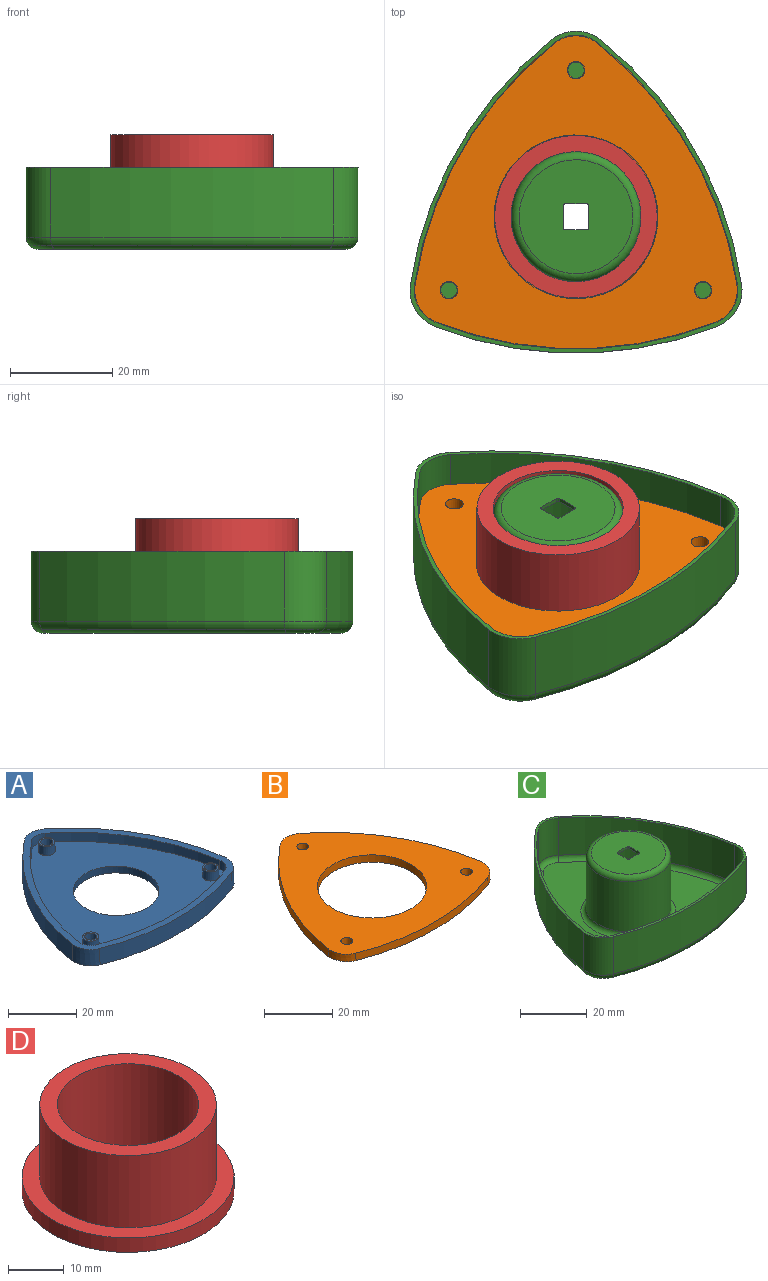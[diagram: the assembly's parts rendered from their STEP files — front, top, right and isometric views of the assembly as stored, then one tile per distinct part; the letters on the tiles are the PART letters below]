
ASSEMBLY  parts=4 mates=3
PART A: 25 faces, bbox 63.3x61.4x5.7 mm
  f0: plane 58.4x56.47mm, normal (0,0,1), area 1717.7mm2, adj f1,f8,f9,f10,f11,f12,f13,f17
  f1: cone r=12.66mm half-angle=3deg, axis (0,0,-1), area 201.3mm2, adj f0,f2
  f2: plane 63.31x61.38mm, normal (0,0,-1), area 2200.2mm2, adj f1,f3,f4,f5,f6,f7,f14,f16
  f3: cone r=6.83mm half-angle=2deg, axis (0,0,-1), area 51.7mm2, adj f2,f4,f14,f15
  f4: cone r=74.46mm half-angle=2deg, axis (0,0,-1), area 319.6mm2, adj f2,f3,f5,f15
  f5: cone r=6.83mm half-angle=2deg, axis (0,0,-1), area 51.7mm2, adj f2,f4,f6,f15
  f6: cone r=74.46mm half-angle=2deg, axis (0,0,-1), area 319.6mm2, adj f2,f5,f7,f15
  f7: cone r=6.83mm half-angle=2deg, axis (0,0,-1), area 51.7mm2, adj f2,f6,f14,f15
  f8: cone r=71.92mm half-angle=2deg, axis (0,0,1), area 172.1mm2, adj f0,f9,f13,f15
  f9: cone r=4.29mm half-angle=2deg, axis (0,0,1), area 18.9mm2, adj f0,f8,f10,f15
  f10: cone r=71.92mm half-angle=2deg, axis (0,0,1), area 172.1mm2, adj f0,f9,f11,f15
  f11: cone r=4.29mm half-angle=2deg, axis (0,0,1), area 18.9mm2, adj f0,f10,f12,f15
  f12: cone r=71.92mm half-angle=2deg, axis (0,0,1), area 172.1mm2, adj f0,f11,f13,f15
  f13: cone r=4.29mm half-angle=2deg, axis (0,0,1), area 18.9mm2, adj f0,f8,f12,f15
  f14: cone r=74.46mm half-angle=2deg, axis (0,0,-1), area 319.6mm2, adj f2,f3,f7,f15
  f15: plane 62.91x60.98mm, normal (0,0,1), area 401.3mm2, adj f3,f4,f5,f6,f7,f8,f9,f10
  f16: cone r=1.59mm half-angle=2deg, axis (0,0,1), area 60.6mm2, adj f2,f18
  f17: cone r=2.54mm half-angle=2deg, axis (0,0,-1), area 47.8mm2, adj f0,f18
  f18: plane 4.68x4.68mm, normal (0,0,1), area 7.2mm2, adj f16,f17
  f19: cone r=1.59mm half-angle=2deg, axis (0,0,1), area 60.6mm2, adj f2,f21
  f20: cone r=2.54mm half-angle=2deg, axis (0,0,-1), area 47.8mm2, adj f0,f21
  f21: plane 4.68x4.68mm, normal (0,0,1), area 7.2mm2, adj f19,f20
  f22: cone r=1.59mm half-angle=2deg, axis (0,0,1), area 60.6mm2, adj f2,f24
  f23: cone r=2.54mm half-angle=2deg, axis (0,0,-1), area 47.8mm2, adj f0,f24
  f24: plane 4.68x4.68mm, normal (0,0,1), area 7.2mm2, adj f22,f23
PART B: 12 faces, bbox 63.3x61.4x2.5 mm
  f0: cone r=6.83mm half-angle=3deg, axis (0,0,-1), area 23.1mm2, adj f1,f5,f10,f11
  f1: cone r=74.46mm half-angle=3deg, axis (0,0,-1), area 142.2mm2, adj f0,f2,f10,f11
  f2: cone r=6.83mm half-angle=3deg, axis (0,0,-1), area 23.1mm2, adj f1,f3,f10,f11
  f3: cone r=74.46mm half-angle=3deg, axis (0,0,-1), area 142.2mm2, adj f2,f4,f10,f11
  f4: cone r=6.83mm half-angle=3deg, axis (0,0,-1), area 23.1mm2, adj f3,f5,f10,f11
  f5: cone r=74.46mm half-angle=3deg, axis (0,0,-1), area 142.2mm2, adj f0,f4,f10,f11
  f6: cone r=1.59mm half-angle=3deg, axis (0,0,1), area 26.4mm2, adj f10,f11
  f7: cone r=1.59mm half-angle=3deg, axis (0,0,1), area 26.4mm2, adj f10,f11
  f8: cone r=1.59mm half-angle=3deg, axis (0,0,1), area 26.4mm2, adj f10,f11
  f9: cone r=15.88mm half-angle=3deg, axis (0,0,1), area 254.8mm2, adj f10,f11
  f10: plane 63.04x61.11mm, normal (0,0,1), area 1868.7mm2, adj f0,f1,f2,f3,f4,f5,f6,f7
  f11: plane 63.31x61.38mm, normal (0,0,-1), area 1912.1mm2, adj f0,f1,f2,f3,f4,f5,f6,f7
PART C: 43 faces, bbox 77x72.4x22.4 mm
  f0: cylinder r=11.91mm len=23.83mm, axis (0,0,-1), area 1380.2mm2, adj f41,f42
  f1: plane 60.16x58.23mm, normal (0,0,1), area 1787.5mm2, adj f16,f17,f18,f19,f20,f21,f40
  f2: cylinder r=7.62mm len=13.67mm, axis (0,0,-1), area 139.8mm2, adj f3,f7,f15,f24
  f3: cylinder r=75.25mm len=55.24mm, axis (0,0,-1), area 772.9mm2, adj f2,f4,f15,f22
  f4: cylinder r=7.62mm len=13.67mm, axis (0,0,-1), area 139.8mm2, adj f3,f5,f15,f23
  f5: cylinder r=75.25mm len=47.84mm, axis (0,0,-1), area 772.9mm2, adj f4,f6,f15,f25
  f6: cylinder r=7.62mm len=13.67mm, axis (0,0,-1), area 139.8mm2, adj f5,f7,f15,f27
  f7: cylinder r=75.25mm len=47.84mm, axis (0,0,-1), area 772.9mm2, adj f2,f6,f15,f26
  f8: plane 60.16x58.23mm, normal (0,0,-1), area 1787.5mm2, adj f22,f23,f24,f25,f26,f27,f42
  f9: cylinder r=74.46mm len=47.33mm, axis (0,0,-1), area 764.8mm2, adj f10,f14,f15,f16
  f10: cylinder r=6.83mm len=13.67mm, axis (0,0,-1), area 125.4mm2, adj f9,f11,f15,f17
  f11: cylinder r=74.46mm len=47.33mm, axis (0,0,-1), area 764.8mm2, adj f10,f12,f15,f19
  f12: cylinder r=6.83mm len=13.67mm, axis (0,0,-1), area 125.4mm2, adj f11,f13,f15,f21
  f13: cylinder r=74.46mm len=54.66mm, axis (0,0,-1), area 764.8mm2, adj f12,f14,f15,f20
  f14: cylinder r=6.83mm len=13.67mm, axis (0,0,-1), area 125.4mm2, adj f9,f13,f15,f18
  f15: plane 64.88x62.95mm, normal (0,0,1), area 155.8mm2, adj f2,f3,f4,f5,f6,f7,f9,f10
  f16: torus R=72.89mm, axis (0,0,1), area 137.4mm2, adj f1,f9,f17,f18
  f17: torus R=5.26mm, axis (0,0,1), area 20.8mm2, adj f1,f10,f16,f19
  f18: torus R=5.26mm, axis (0,0,1), area 20.8mm2, adj f1,f14,f16,f20
  f19: torus R=72.89mm, axis (0,0,1), area 137.4mm2, adj f1,f11,f17,f21
  f20: torus R=72.89mm, axis (0,0,1), area 137.4mm2, adj f1,f13,f18,f21
  f21: torus R=5.26mm, axis (0,0,1), area 20.8mm2, adj f1,f12,f19,f20
  f22: torus R=72.89mm, axis (0,0,1), area 207.5mm2, adj f3,f8,f23,f24
  f23: torus R=5.26mm, axis (0,0,1), area 33.7mm2, adj f4,f8,f22,f25
  f24: torus R=5.26mm, axis (0,0,1), area 33.7mm2, adj f2,f8,f22,f26
  f25: torus R=72.89mm, axis (0,0,1), area 207.5mm2, adj f5,f8,f23,f27
  f26: torus R=72.89mm, axis (0,0,1), area 207.5mm2, adj f7,f8,f24,f27
  f27: torus R=5.26mm, axis (0,0,1), area 33.7mm2, adj f6,f8,f25,f26
  f28: cylinder r=12.7mm len=25.4mm, axis (0,0,-1), area 1471.5mm2, adj f39,f40
  f29: plane 22.25x22.25mm, normal (0,0,1), area 363.3mm2, adj f30,f31,f32,f33,f34,f35,f36,f37
  f30: cylinder r=0.51mm len=0.79mm, axis (0,0,-1), area 0.6mm2, adj f29,f31,f37,f38
  f31: plane 4.06x0.79mm, normal (-1,0,0), area 3.2mm2, adj f29,f30,f32,f38
  f32: cylinder r=0.51mm len=0.79mm, axis (0,0,-1), area 0.6mm2, adj f29,f31,f33,f38
  f33: plane 4.06x0.79mm, normal (0,1,0), area 3.2mm2, adj f29,f32,f34,f38
  f34: cylinder r=0.51mm len=0.79mm, axis (0,0,-1), area 0.6mm2, adj f29,f33,f35,f38
  f35: plane 4.06x0.79mm, normal (1,0,0), area 3.2mm2, adj f29,f34,f36,f38
  f36: cylinder r=0.51mm len=0.79mm, axis (0,0,-1), area 0.6mm2, adj f29,f35,f37,f38
  f37: plane 4.06x0.79mm, normal (0,-1,0), area 3.2mm2, adj f29,f30,f36,f38
  f38: plane 22.25x22.25mm, normal (0,0,-1), area 363.3mm2, adj f30,f31,f32,f33,f34,f35,f36,f37
  f39: torus R=11.13mm, axis (0,0,1), area 188.5mm2, adj f28,f29
  f40: torus R=14.27mm, axis (0,0,1), area 206.3mm2, adj f1,f28
  f41: torus R=11.13mm, axis (0,0,1), area 90.4mm2, adj f0,f38
  f42: torus R=14.27mm, axis (0,0,1), area 297.7mm2, adj f0,f8
PART D: 6 faces, bbox 38.1x38.1x19.1 mm
  f0: cylinder r=12.7mm len=25.4mm, axis (0,0,-1), area 1520.1mm2, adj f2,f3
  f1: cylinder r=15.88mm len=31.75mm, axis (0,0,-1), area 1583.5mm2, adj f2,f5
  f2: plane 31.75x31.75mm, normal (0,0,1), area 285mm2, adj f0,f1
  f3: plane 38.1x38.1mm, normal (0,0,-1), area 633.4mm2, adj f0,f4
  f4: cylinder r=19.05mm len=38.1mm, axis (0,0,-1), area 380mm2, adj f3,f5
  f5: plane 38.1x38.1mm, normal (0,0,1), area 348.4mm2, adj f1,f4
PLACE A t=(-41.37,56.25,-42.86)mm
PLACE B t=(12.67,145.08,-37.15)mm
PLACE C t=(-116.41,141.58,-43.65)mm
PLACE D t=(166.27,99.05,-40.32)mm
MATE fastened B.f9 <-> D.f0  axis (0,0,-1) through (98.6,37.46,-37.15)mm
MATE fastened A.f3 <-> B.f0  axis (0,0,1) through (98.6,66.12,-37.15)mm
MATE fastened C.f0 <-> A.f1  axis (0,0,1) through (98.6,37.46,-42.86)mm
